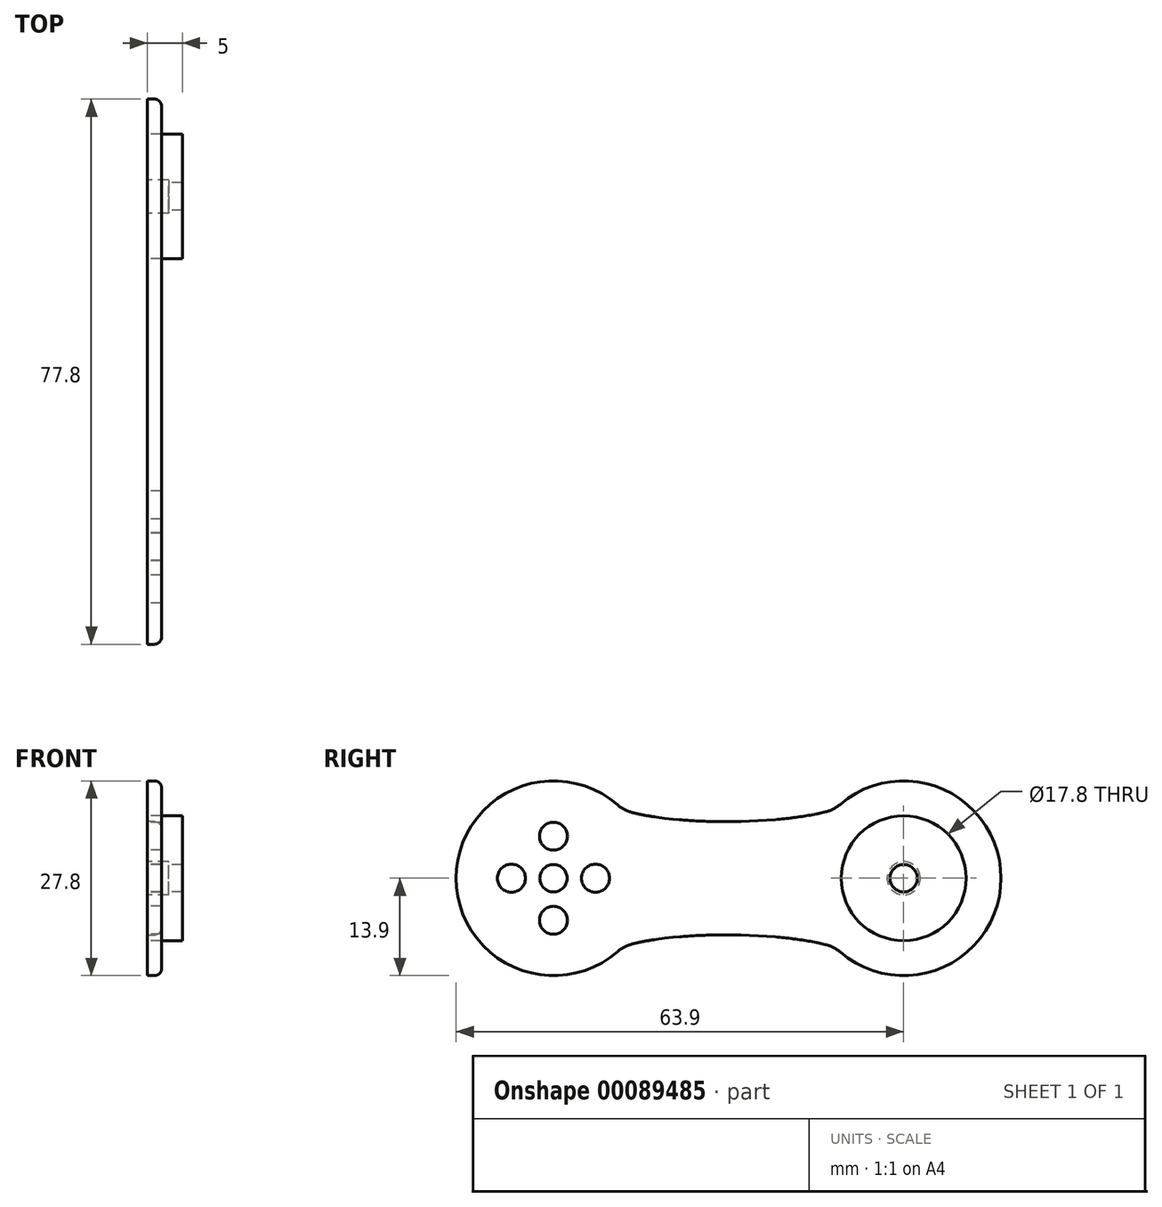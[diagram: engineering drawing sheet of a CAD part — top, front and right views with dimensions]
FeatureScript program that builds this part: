
annotation { "Feature Type Name" : "Feature", "Feature Type Description" : "" }
export const myFeature = defineFeature(function(context is Context, id is Id, definition is map)
    precondition{}
    {
        {
            var Q0;
            Q0=qCreatedBy(makeId("Right.planeOp"),FACE);
            var sketch = newSketch(context, id + "F0", { "sketchPlane" : qUnion([Q0])});
            skCircle(sketch, "E0", {"center": v(0, 0) * mm, "radius": 8.9 * mm});
            skLineSegment(sketch, "E1", {"start": v(0, 0) * mm, "end": v(50, 0) * mm, "construction": true});
            skCircle(sketch, "E2", {"center": v(50, 0) * mm, "radius": 8.9 * mm});
            skCircle(sketch, "E3.0", {"center": v(0, 0) * mm, "radius": 13.9 * mm});
            skCircle(sketch, "E4.0", {"center": v(50, 0) * mm, "radius": 13.9 * mm});
            skLineSegment(sketch, "E5", {"start": v(0, 0) * mm, "end": v(9.83, 9.83) * mm, "construction": true});
            skLineSegment(sketch, "E6", {"start": v(50, 0) * mm, "end": v(40.17, 9.83) * mm, "construction": true});
            skLineSegment(sketch, "E7", {"start": v(0, 0) * mm, "end": v(9.83, -9.83) * mm, "construction": true});
            skLineSegment(sketch, "E8", {"start": v(50, 0) * mm, "end": v(40.17, -9.83) * mm, "construction": true});
            skLineSegment(sketch, "E9", {"start": v(9.83, 9.83) * mm, "end": v(40.17, 9.83) * mm, "construction": true});
            skFitSpline(sketch, "E10", {"points": [v(9.83, 9.83) * mm, v(40.17, 9.83) * mm], "startDerivative": vector(19.25, -6.99) * mm, "endDerivative": vector(22.48, 6.99) * mm});
            skFitSpline(sketch, "E11", {"points": [v(9.83, -9.83) * mm, v(40.17, -9.83) * mm], "startDerivative": vector(19.25, 6.99) * mm, "endDerivative": vector(22.48, -6.99) * mm});
            skLineSegment(sketch, "E12", {"start": v(16.25, 7.5) * mm, "end": v(16.25, -7.5) * mm});
            skLineSegment(sketch, "E13", {"start": v(32.68, 7.5) * mm, "end": v(32.68, -7.5) * mm});
            skCircle(sketch, "E14", {"center": v(0, 0) * mm, "radius": 2.38 * mm});
            skCircle(sketch, "E15", {"center": v(0, 0) * mm, "radius": 1.25 * mm});
            skCircle(sketch, "E16", {"center": v(0, 0) * mm, "radius": 1.95 * mm});
            skCircle(sketch, "E17", {"center": v(50, 0) * mm, "radius": 2.38 * mm});
            skCircle(sketch, "E18", {"center": v(50, 0) * mm, "radius": 1.25 * mm});
            skCircle(sketch, "E19", {"center": v(50, 0) * mm, "radius": 1.95 * mm});
            skSolve(sketch);
        }
        {
            var Q0;
            Q0=makeQuery(id+"F0.imprint","IMPRINT",FACE,{"disambiguationData":[TD([[makeQuery(id+"F0.imprint","IMPRINT",EDGE,{"derivedFrom":sQuery(id+"F0.wireOp",EDGE,"E2")}),1.0]])]});
            var Q1;
            Q1=makeQuery(id+"F0.imprint","IMPRINT",FACE,{"disambiguationData":[TD([[makeQuery(id+"F0.imprint","IMPRINT",EDGE,{"derivedFrom":sQuery(id+"F0.wireOp",EDGE,"E17")}),1.0]])]});
            extrude(context, id + "F1", {"entities" : qUnion([Q0, Q1]), "depth" : 5 * mm});
        }
        {
            var Q0;
            Q0=makeQuery(id+"F0.imprint","IMPRINT",FACE,{"disambiguationData":[TD([[makeQuery(id+"F0.imprint","IMPRINT",EDGE,{"derivedFrom":sQuery(id+"F0.wireOp",EDGE,"E0")}),-1.0]])]});
            var Q1;
            {var subQ0=sQuery(id+"F0.wireOp",EDGE,"E10");Q1=makeQuery(id+"F0.imprint","IMPRINT",FACE,{"disambiguationData":[TD([[makeQuery(id+"F0.imprint","IMPRINT",EDGE,{"derivedFrom":subQ0}),-1.0]])]});}
            var Q2;
            Q2=makeQuery(id+"F0.imprint","IMPRINT",FACE,{"disambiguationData":[TD([[makeQuery(id+"F0.imprint","IMPRINT",EDGE,{"derivedFrom":sQuery(id+"F0.wireOp",EDGE,"E2")}),-1.0]])]});
            extrude(context, id + "F2", {"entities" : qUnion([Q0, Q1, Q2]), "depth" : 2 * mm});
        }
        {
            var Q0;
            Q0=makeQuery(id+"F0.imprint","IMPRINT",FACE,{"disambiguationData":[TD([[makeQuery(id+"F0.imprint","IMPRINT",EDGE,{"derivedFrom":sQuery(id+"F0.wireOp",EDGE,"E0")}),1.0]])]});
            var Q1;
            Q1=makeQuery(id+"F0.imprint","IMPRINT",FACE,{"disambiguationData":[TD([[makeQuery(id+"F0.imprint","IMPRINT",EDGE,{"derivedFrom":sQuery(id+"F0.wireOp",EDGE,"E14")}),1.0]])]});
            extrude(context, id + "F3", {"entities" : qUnion([Q0, Q1]), "operationType" : NewBodyOperationType.ADD, "depth" : 2 * mm});
        }
        {
            var Q0;
            Q0=makeQuery(id+"F2.opExtrude","SWEPT_EDGE",EDGE,{"disambiguationData":[OSD([sQuery(id+"F0.wireOp",EDGE,"E3.0"),sQuery(id+"F0.wireOp",EDGE,"E10")])]});
            var Q1;
            Q1=makeQuery(id+"F2.opExtrude","SWEPT_EDGE",EDGE,{"disambiguationData":[OSD([sQuery(id+"F0.wireOp",EDGE,"E4.0"),sQuery(id+"F0.wireOp",EDGE,"E10")])]});
            var Q2;
            Q2=makeQuery(id+"F2.opExtrude","SWEPT_EDGE",EDGE,{"disambiguationData":[OSD([sQuery(id+"F0.wireOp",EDGE,"E3.0"),sQuery(id+"F0.wireOp",EDGE,"E11")])]});
            var Q3;
            Q3=makeQuery(id+"F2.opExtrude","SWEPT_EDGE",EDGE,{"disambiguationData":[OSD([sQuery(id+"F0.wireOp",EDGE,"E4.0"),sQuery(id+"F0.wireOp",EDGE,"E11")])]});
            fillet(context, id + "F4", {"entities" : qUnion([Q0, Q1, Q2, Q3]), "radius" : 5 * mm, "tangentPropagation" : true, "allowEdgeOverflow" : false});
        }
        {
            var Q0;
            Q0=makeQuery(id+"F2.opExtrude","CAP_EDGE",EDGE,{"disambiguationData":[OSD([sQuery(id+"F0.wireOp",EDGE,"E4.0")])],"isStart":false});
            var Q1;
            Q1=makeQuery(id+"F2.opExtrude","CAP_EDGE",EDGE,{"disambiguationData":[OSD([sQuery(id+"F0.wireOp",EDGE,"E10")])],"isStart":false});
            var Q2;
            Q2=makeQuery(id+"F2.opExtrude","CAP_EDGE",EDGE,{"disambiguationData":[OSD([sQuery(id+"F0.wireOp",EDGE,"E3.0")])],"isStart":false});
            var Q3;
            Q3=makeQuery(id+"F2.opExtrude","CAP_EDGE",EDGE,{"disambiguationData":[OSD([sQuery(id+"F0.wireOp",EDGE,"E11")])],"isStart":false});
            fillet(context, id + "F5", {"entities" : qUnion([Q0, Q1, Q2, Q3]), "radius" : 1 * mm, "tangentPropagation" : true, "allowEdgeOverflow" : false});
        }
        {
            var Q0;
            Q0=qCreatedBy(makeId("Right.planeOp"),FACE);
            var sketch = newSketch(context, id + "F6", { "sketchPlane" : qUnion([Q0])});
            skPoint(sketch, "E20.center", {"position": v(0, 0) * mm});
            skLineSegment(sketch, "E21.rect.right", {"start": v(9, -12) * mm, "end": v(-27, -12) * mm});
            skCircle(sketch, "E22", {"center": v(-24, 6) * mm, "radius": 2 * mm});
            skLineSegment(sketch, "E23", {"start": v(-27, 0) * mm, "end": v(9, 0) * mm, "construction": true});
            skCircle(sketch, "E24", {"center": v(0, 0) * mm, "radius": 8.9 * mm});
            skLineSegment(sketch, "E21.rect.left", {"start": v(9, 12) * mm, "end": v(-27, 12) * mm});
            skLineSegment(sketch, "E21.rect.bottom", {"start": v(9, 12) * mm, "end": v(9, -12) * mm});
            skLineSegment(sketch, "E21.rect.top", {"start": v(-27, 12) * mm, "end": v(-27, -12) * mm});
            skLineSegment(sketch, "E25", {"start": v(-24, -6) * mm, "end": v(-24, 6) * mm, "construction": true});
            skCircle(sketch, "E26", {"center": v(-24, 0) * mm, "radius": 2 * mm});
            skPoint(sketch, "E21.rect.middle", {"position": v(-9, 0) * mm});
            skCircle(sketch, "E20.2.0", {"center": v(-6, 0) * mm, "radius": 2 * mm});
            skCircle(sketch, "E20.1.0", {"center": v(0, 6) * mm, "radius": 2 * mm});
            skCircle(sketch, "E27", {"center": v(0, 0) * mm, "radius": 6 * mm, "construction": true});
            skCircle(sketch, "E28", {"center": v(6, 0) * mm, "radius": 2 * mm});
            skCircle(sketch, "E29", {"center": v(-4.24, -4.24) * mm, "radius": 0.8 * mm});
            skCircle(sketch, "E20.3.0", {"center": v(0, -6) * mm, "radius": 2 * mm});
            skCircle(sketch, "E30.3.0", {"center": v(-4.24, 4.24) * mm, "radius": 0.8 * mm});
            skCircle(sketch, "E30.2.0", {"center": v(4.24, 4.24) * mm, "radius": 0.8 * mm});
            skCircle(sketch, "E30.1.0", {"center": v(4.24, -4.24) * mm, "radius": 0.8 * mm});
            skCircle(sketch, "E31", {"center": v(-24, -6) * mm, "radius": 2 * mm});
            skSolve(sketch);
        }
        {
            var Q0;
            Q0=makeQuery(id+"F6.imprint","IMPRINT",FACE,{"disambiguationData":[TD([[makeQuery(id+"F6.imprint","IMPRINT",EDGE,{"derivedFrom":sQuery(id+"F6.wireOp",EDGE,"E28")}),1.0]])]});
            var Q1;
            Q1=makeQuery(id+"F6.imprint","IMPRINT",FACE,{"disambiguationData":[TD([[makeQuery(id+"F6.imprint","IMPRINT",EDGE,{"derivedFrom":sQuery(id+"F6.wireOp",EDGE,"E20.2.0")}),1.0]])]});
            var Q2;
            Q2=makeQuery(id+"F6.imprint","IMPRINT",FACE,{"disambiguationData":[TD([[makeQuery(id+"F6.imprint","IMPRINT",EDGE,{"derivedFrom":sQuery(id+"F6.wireOp",EDGE,"E20.1.0")}),1.0]])]});
            var Q3;
            Q3=makeQuery(id+"F6.imprint","IMPRINT",FACE,{"disambiguationData":[TD([[makeQuery(id+"F6.imprint","IMPRINT",EDGE,{"derivedFrom":sQuery(id+"F6.wireOp",EDGE,"E20.3.0")}),1.0]])]});
            var Q4;
            Q4=sQuery(id+"F6.wireOp",EDGE,"E20.1.0");
            var Q5;
            Q5=sQuery(id+"F6.wireOp",EDGE,"E30.3.0");
            var Q6;
            Q6=sQuery(id+"F6.wireOp",EDGE,"E20.2.0");
            var Q7;
            Q7=sQuery(id+"F6.wireOp",EDGE,"E29");
            var Q8;
            Q8=sQuery(id+"F6.wireOp",EDGE,"E20.3.0");
            var Q9;
            Q9=sQuery(id+"F6.wireOp",EDGE,"E28");
            var Q10;
            Q10=sQuery(id+"F6.wireOp",EDGE,"E30.1.0");
            var Q11;
            Q11=sQuery(id+"F6.wireOp",EDGE,"E30.2.0");
            extrude(context, id + "F7", {"entities" : qUnion([Q0, Q1, Q2, Q3]), "operationType" : NewBodyOperationType.REMOVE, "surfaceEntities" : qUnion([Q4, Q5, Q6, Q7, Q8, Q9, Q10, Q11]), "endBound" : BoundingType.SYMMETRIC, "depth" : 25 * mm});
        }
        {
            var Q0;
            Q0=makeQuery(id+"F0.imprint","IMPRINT",FACE,{"disambiguationData":[TD([[makeQuery(id+"F0.imprint","IMPRINT",EDGE,{"derivedFrom":sQuery(id+"F0.wireOp",EDGE,"E17")}),1.0]])]});
            extrude(context, id + "F8", {"entities" : qUnion([Q0]), "operationType" : NewBodyOperationType.REMOVE, "depth" : 3 * mm});
        }
    });
